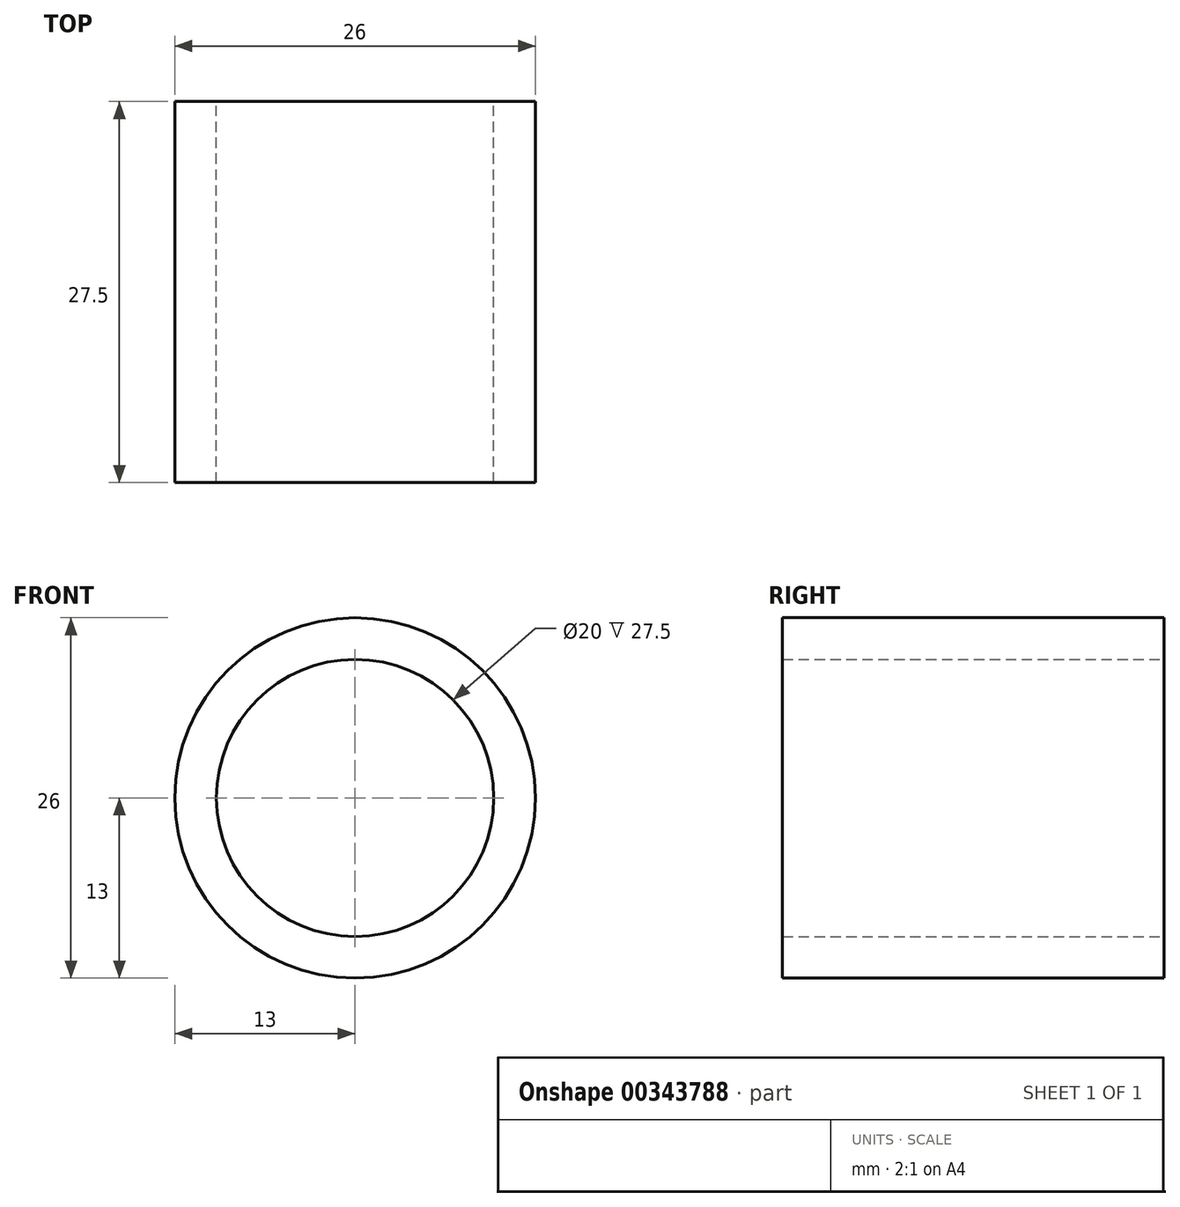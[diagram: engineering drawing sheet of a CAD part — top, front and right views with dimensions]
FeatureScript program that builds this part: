
annotation { "Feature Type Name" : "Feature", "Feature Type Description" : "" }
export const myFeature = defineFeature(function(context is Context, id is Id, definition is map)
    precondition{}
    {
        {
            var Q0;
            Q0=qCreatedBy(makeId("Front.planeOp"),FACE);
            var sketch = newSketch(context, id + "F0", { "sketchPlane" : qUnion([Q0])});
            skCircle(sketch, "E0", {"center": v(0, 0) * mm, "radius": 13 * mm});
            skCircle(sketch, "E1", {"center": v(0, 0) * mm, "radius": 10 * mm});
            skSolve(sketch);
        }
        {
            var Q0;
            Q0=makeQuery(id+"F0.imprint","IMPRINT",FACE,{"disambiguationData":[TD([[makeQuery(id+"F0.imprint","IMPRINT",EDGE,{"derivedFrom":sQuery(id+"F0.wireOp",EDGE,"E0")}),1.0]])]});
            extrude(context, id + "F1", {"entities" : qUnion([Q0]), "depth" : 27.5 * mm, "offsetDistance" : 25 * mm, "symmetric" : true});
        }
    });
